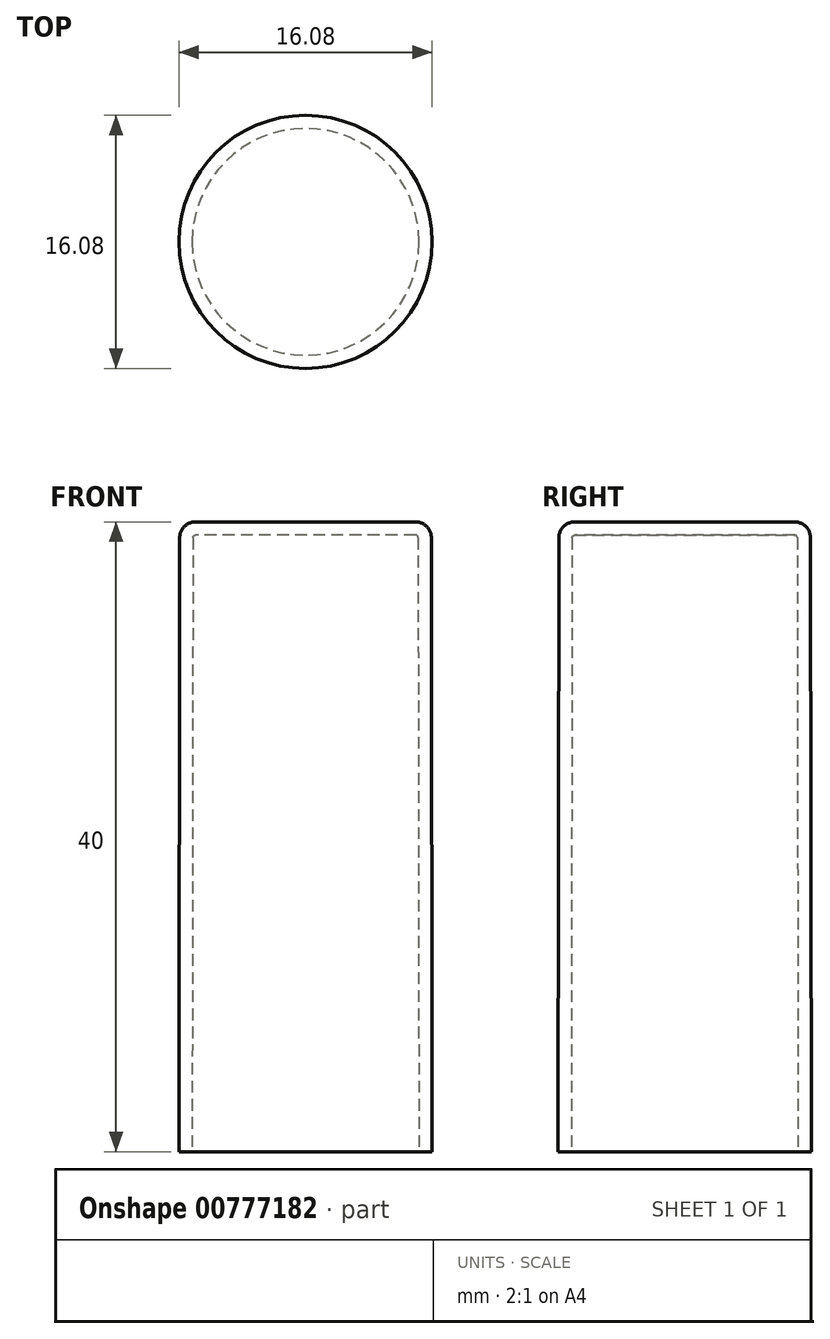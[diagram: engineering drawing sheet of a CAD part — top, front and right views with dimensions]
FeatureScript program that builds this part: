
annotation { "Feature Type Name" : "Feature", "Feature Type Description" : "" }
export const myFeature = defineFeature(function(context is Context, id is Id, definition is map)
    precondition{}
    {
        {
            assignVariable(context, id + "F0", {"name" : "thickness", "anyValue" : 0.42 * 2});
        }
        {
            var Q0;
            Q0=qCreatedBy(makeId("Top.planeOp"),FACE);
            var sketch = newSketch(context, id + "F1", { "sketchPlane" : qUnion([Q0])});
            skCircle(sketch, "E0", {"center": v(0, 0) * mm, "radius": 8.04 * mm});
            skSolve(sketch);
        }
        {
            var Q0;
            Q0=qCreatedBy(makeId("Top.planeOp"),FACE);
            cPlane(context, id + "F2", {"entities" : qUnion([Q0]), "cplaneType" : CPlaneType.OFFSET, "offset" : 40 * mm, "width" : 150 * mm, "height" : 150 * mm});
        }
        {
            var Q0;
            Q0=qCreatedBy(id+"F2.planeOp",FACE);
            var sketch = newSketch(context, id + "F3", { "sketchPlane" : qUnion([Q0])});
            skCircle(sketch, "E1", {"center": v(0, 0) * mm, "radius": 8 * mm});
            skSolve(sketch);
        }
        {
            var Q0;
            Q0=makeQuery(id+"F1.imprint","IMPRINT",FACE,{"disambiguationData":[TD([[makeQuery(id+"F1.imprint","IMPRINT",EDGE,{"derivedFrom":sQuery(id+"F1.wireOp",EDGE,"E0")}),1.0]])]});
            var Q1;
            Q1=makeQuery(id+"F3.imprint","IMPRINT",FACE,{"disambiguationData":[TD([[makeQuery(id+"F3.imprint","IMPRINT",EDGE,{"derivedFrom":sQuery(id+"F3.wireOp",EDGE,"E1")}),1.0]])]});
            loft(context, id + "F4", {"sheetProfilesArray" : [{ "sheetProfileEntities" : qUnion([Q0]) }, { "sheetProfileEntities" : qUnion([Q1]) }]});
        }
        {
            var Q0;
            Q0=makeQuery(id+"F4.opLoft","MID_CAP_EDGE",EDGE,{"disambiguationData":[OSD([sQuery(id+"F3.wireOp",EDGE,"E1")])],"capPos":1.0});
            fillet(context, id + "F5", {"entities" : qUnion([Q0]), "radius" : 1 * mm, "tangentPropagation" : true, "allowEdgeOverflow" : false});
        }
        {
            var Q0;
            Q0=makeQuery(id+"F4.opLoft","CAP_FACE",FACE,{"disambiguationData":[OSD([makeQuery(id+"F1.imprint","IMPRINT",FACE,{"disambiguationData":[TD([[makeQuery(id+"F1.imprint","IMPRINT",EDGE,{"derivedFrom":sQuery(id+"F1.wireOp",EDGE,"E0")}),1.0]])]})])],"isStart":true});
            shell(context, id + "F6", {"entities" : qUnion([Q0]), "thickness" : (getVariable(context, 'thickness')) * mm});
        }
    });
